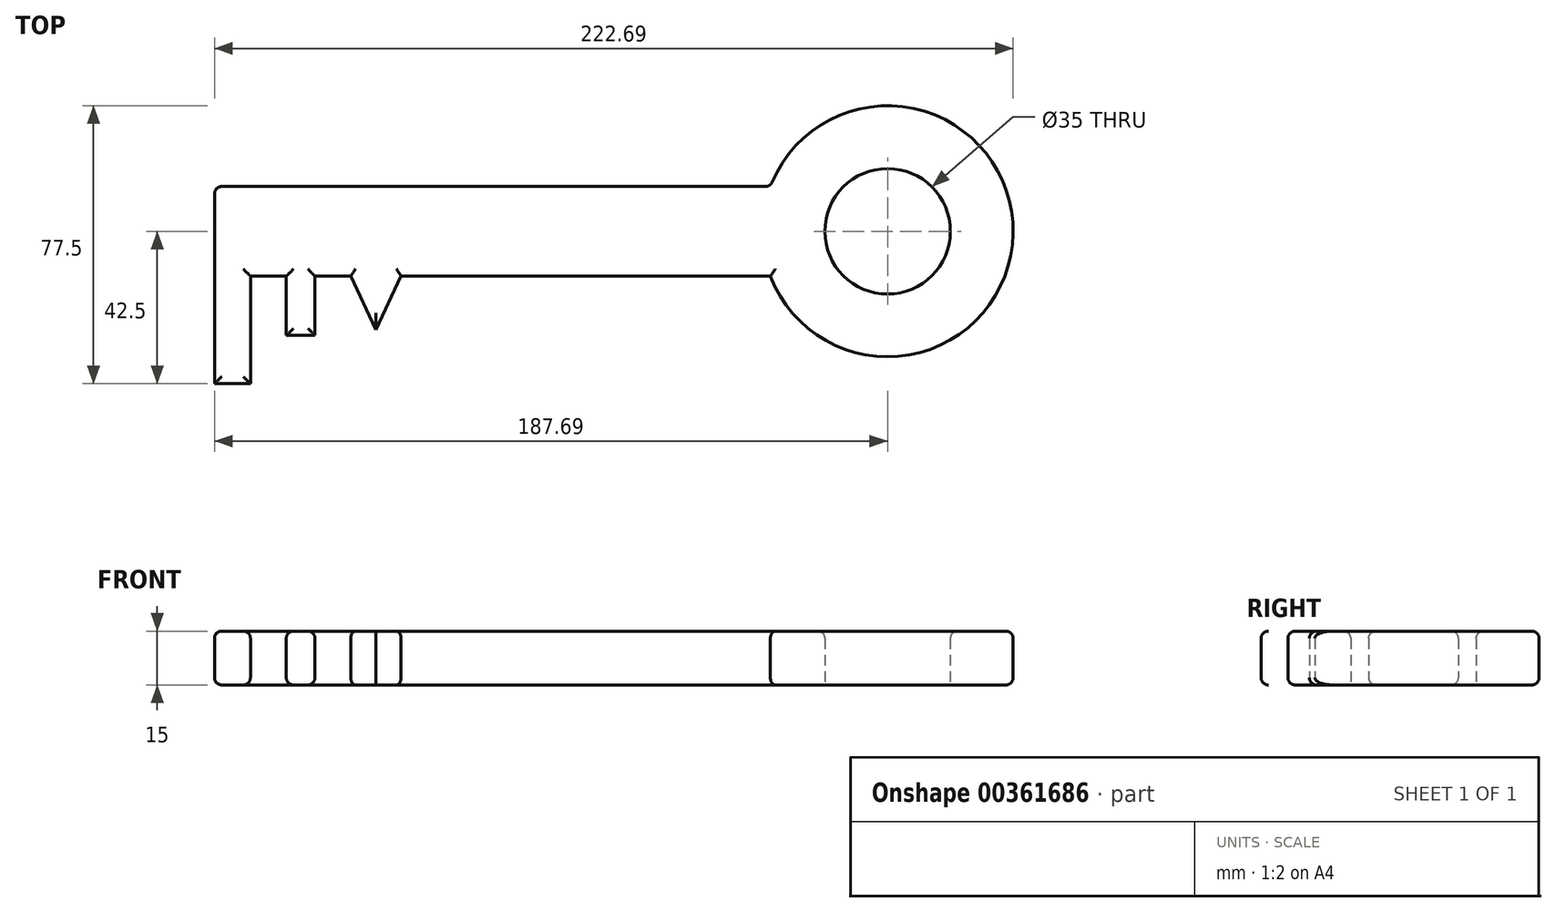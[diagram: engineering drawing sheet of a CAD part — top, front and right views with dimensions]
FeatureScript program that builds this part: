
annotation { "Feature Type Name" : "Feature", "Feature Type Description" : "" }
export const myFeature = defineFeature(function(context is Context, id is Id, definition is map)
    precondition{}
    {
        {
            var Q0;
            Q0=qCreatedBy(makeId("Top.planeOp"),FACE);
            var sketch = newSketch(context, id + "F0", { "sketchPlane" : qUnion([Q0])});
            skLineSegment(sketch, "E0.bottom", {"start": v(-68.81, 25) * mm, "end": v(86.19, 25) * mm});
            skLineSegment(sketch, "E0.top", {"start": v(-58.81, 0) * mm, "end": v(-48.81, 0) * mm});
            skLineSegment(sketch, "E0.left", {"start": v(-68.81, 25) * mm, "end": v(-68.81, 0) * mm});
            skLineSegment(sketch, "E1.top", {"start": v(-68.81, -30) * mm, "end": v(-58.81, -30) * mm});
            skLineSegment(sketch, "E1.left", {"start": v(-68.81, 0) * mm, "end": v(-68.81, -30) * mm});
            skLineSegment(sketch, "E1.right", {"start": v(-58.81, 0) * mm, "end": v(-58.81, -30) * mm});
            skLineSegment(sketch, "E2.top", {"start": v(-48.81, -16.55) * mm, "end": v(-40.81, -16.55) * mm});
            skLineSegment(sketch, "E2.left", {"start": v(-48.81, 0) * mm, "end": v(-48.81, -16.55) * mm});
            skLineSegment(sketch, "E2.right", {"start": v(-40.81, 0) * mm, "end": v(-40.81, -16.55) * mm});
            skArc(sketch, "E3", {"start": v(86.19, 0) * mm, "mid": v(153.88, 12.5) * mm, "end": v(86.19, 25) * mm});
            skCircle(sketch, "E4", {"center": v(118.88, 12.5) * mm, "radius": 17.5 * mm});
            skLineSegment(sketch, "E5", {"start": v(-16.81, 0) * mm, "end": v(-23.81, -15) * mm});
            skLineSegment(sketch, "E6", {"start": v(-30.81, 0) * mm, "end": v(-23.81, -15) * mm});
            skLineSegment(sketch, "E7", {"start": v(118.88, 12.5) * mm, "end": v(-68.81, 12.5) * mm, "construction": true});
            skLineSegment(sketch, "E8.trimOffspring", {"start": v(-40.81, 0) * mm, "end": v(-30.81, 0) * mm});
            skLineSegment(sketch, "E9.trimOffspring", {"start": v(-16.81, 0) * mm, "end": v(86.19, 0) * mm});
            skLineSegment(sketch, "E10", {"start": v(-30.81, 0) * mm, "end": v(-16.81, 0) * mm, "construction": true});
            skLineSegment(sketch, "E11", {"start": v(-23.81, -15) * mm, "end": v(-23.81, 0) * mm, "construction": true});
            skSolve(sketch);
        }
        {
            var Q0;
            Q0=makeQuery(id+"F0.imprint","IMPRINT",FACE,{"disambiguationData":[TD([[makeQuery(id+"F0.imprint","IMPRINT",EDGE,{"derivedFrom":sQuery(id+"F0.wireOp",EDGE,"E0.bottom")}),-1.0]])]});
            extrude(context, id + "F1", {"entities" : qUnion([Q0]), "depth" : 15 * mm});
        }
        {
            var Q0;
            Q0=makeQuery(id+"F1.opExtrude","CAP_EDGE",EDGE,{"disambiguationData":[OSD([sQuery(id+"F0.wireOp",EDGE,"E0.bottom")])],"isStart":false});
            var Q1;
            Q1=makeQuery(id+"F1.opExtrude","CAP_EDGE",EDGE,{"disambiguationData":[OSD([sQuery(id+"F0.wireOp",EDGE,"E0.left"),sQuery(id+"F0.wireOp",EDGE,"E1.left")])],"isStart":false});
            var Q2;
            Q2=makeQuery(id+"F1.opExtrude","CAP_EDGE",EDGE,{"disambiguationData":[OSD([sQuery(id+"F0.wireOp",EDGE,"E1.right")])],"isStart":false});
            var Q3;
            Q3=makeQuery(id+"F1.opExtrude","CAP_EDGE",EDGE,{"disambiguationData":[OSD([sQuery(id+"F0.wireOp",EDGE,"E2.left")])],"isStart":false});
            var Q4;
            Q4=makeQuery(id+"F1.opExtrude","CAP_EDGE",EDGE,{"disambiguationData":[OSD([sQuery(id+"F0.wireOp",EDGE,"E2.top")])],"isStart":false});
            var Q5;
            Q5=makeQuery(id+"F1.opExtrude","CAP_EDGE",EDGE,{"disambiguationData":[OSD([sQuery(id+"F0.wireOp",EDGE,"E6")])],"isStart":false});
            var Q6;
            Q6=makeQuery(id+"F1.opExtrude","CAP_EDGE",EDGE,{"disambiguationData":[OSD([sQuery(id+"F0.wireOp",EDGE,"E9.trimOffspring")])],"isStart":false});
            var Q7;
            Q7=makeQuery(id+"F1.opExtrude","CAP_EDGE",EDGE,{"disambiguationData":[OSD([sQuery(id+"F0.wireOp",EDGE,"E5")])],"isStart":false});
            var Q8;
            Q8=makeQuery(id+"F1.opExtrude","CAP_EDGE",EDGE,{"disambiguationData":[OSD([sQuery(id+"F0.wireOp",EDGE,"E2.right")])],"isStart":false});
            var Q9;
            Q9=makeQuery(id+"F1.opExtrude","CAP_EDGE",EDGE,{"disambiguationData":[OSD([sQuery(id+"F0.wireOp",EDGE,"E1.top")])],"isStart":false});
            var Q10;
            Q10=makeQuery(id+"F1.opExtrude","CAP_FACE",FACE,{"disambiguationData":[OSD([sQuery(id+"F0.wireOp",EDGE,"E0.bottom"),sQuery(id+"F0.wireOp",EDGE,"E0.top"),sQuery(id+"F0.wireOp",EDGE,"E0.left"),sQuery(id+"F0.wireOp",EDGE,"E1.top"),sQuery(id+"F0.wireOp",EDGE,"E1.left"),sQuery(id+"F0.wireOp",EDGE,"E1.right"),sQuery(id+"F0.wireOp",EDGE,"E2.top"),sQuery(id+"F0.wireOp",EDGE,"E2.left"),sQuery(id+"F0.wireOp",EDGE,"E2.right"),sQuery(id+"F0.wireOp",EDGE,"E3"),sQuery(id+"F0.wireOp",EDGE,"E4"),sQuery(id+"F0.wireOp",EDGE,"E5"),sQuery(id+"F0.wireOp",EDGE,"E6"),sQuery(id+"F0.wireOp",EDGE,"E8.trimOffspring"),sQuery(id+"F0.wireOp",EDGE,"E9.trimOffspring")])],"isStart":false});
            var Q11;
            Q11=makeQuery(id+"F1.opExtrude","CAP_EDGE",EDGE,{"disambiguationData":[OSD([sQuery(id+"F0.wireOp",EDGE,"E4")])],"isStart":false});
            var Q12;
            Q12=makeQuery(id+"F1.opExtrude","CAP_EDGE",EDGE,{"disambiguationData":[OSD([sQuery(id+"F0.wireOp",EDGE,"E3")])],"isStart":false});
            var Q13;
            Q13=makeQuery(id+"F1.opExtrude","CAP_EDGE",EDGE,{"disambiguationData":[OSD([sQuery(id+"F0.wireOp",EDGE,"E3")])],"isStart":true});
            var Q14;
            Q14=makeQuery(id+"F1.opExtrude","CAP_EDGE",EDGE,{"disambiguationData":[OSD([sQuery(id+"F0.wireOp",EDGE,"E0.bottom")])],"isStart":true});
            var Q15;
            Q15=makeQuery(id+"F1.opExtrude","SWEPT_EDGE",EDGE,{"disambiguationData":[OSD([sQuery(id+"F0.wireOp",EDGE,"E0.bottom"),sQuery(id+"F0.wireOp",EDGE,"E3")])]});
            var Q16;
            Q16=makeQuery(id+"F1.opExtrude","SWEPT_EDGE",EDGE,{"disambiguationData":[OSD([sQuery(id+"F0.wireOp",EDGE,"E0.bottom"),sQuery(id+"F0.wireOp",EDGE,"E0.left")])]});
            var Q17;
            Q17=makeQuery(id+"F1.opExtrude","CAP_EDGE",EDGE,{"disambiguationData":[OSD([sQuery(id+"F0.wireOp",EDGE,"E9.trimOffspring")])],"isStart":true});
            var Q18;
            Q18=makeQuery(id+"F1.opExtrude","CAP_EDGE",EDGE,{"disambiguationData":[OSD([sQuery(id+"F0.wireOp",EDGE,"E5")])],"isStart":true});
            var Q19;
            Q19=makeQuery(id+"F1.opExtrude","CAP_EDGE",EDGE,{"disambiguationData":[OSD([sQuery(id+"F0.wireOp",EDGE,"E6")])],"isStart":true});
            var Q20;
            Q20=makeQuery(id+"F1.opExtrude","CAP_EDGE",EDGE,{"disambiguationData":[OSD([sQuery(id+"F0.wireOp",EDGE,"E8.trimOffspring")])],"isStart":true});
            var Q21;
            Q21=makeQuery(id+"F1.opExtrude","CAP_EDGE",EDGE,{"disambiguationData":[OSD([sQuery(id+"F0.wireOp",EDGE,"E2.right")])],"isStart":true});
            var Q22;
            Q22=makeQuery(id+"F1.opExtrude","CAP_EDGE",EDGE,{"disambiguationData":[OSD([sQuery(id+"F0.wireOp",EDGE,"E2.top")])],"isStart":true});
            var Q23;
            Q23=makeQuery(id+"F1.opExtrude","CAP_EDGE",EDGE,{"disambiguationData":[OSD([sQuery(id+"F0.wireOp",EDGE,"E2.left")])],"isStart":true});
            var Q24;
            Q24=makeQuery(id+"F1.opExtrude","CAP_EDGE",EDGE,{"disambiguationData":[OSD([sQuery(id+"F0.wireOp",EDGE,"E0.top")])],"isStart":true});
            var Q25;
            Q25=makeQuery(id+"F1.opExtrude","CAP_EDGE",EDGE,{"disambiguationData":[OSD([sQuery(id+"F0.wireOp",EDGE,"E1.right")])],"isStart":true});
            var Q26;
            Q26=makeQuery(id+"F1.opExtrude","CAP_EDGE",EDGE,{"disambiguationData":[OSD([sQuery(id+"F0.wireOp",EDGE,"E1.top")])],"isStart":true});
            var Q27;
            Q27=makeQuery(id+"F1.opExtrude","CAP_EDGE",EDGE,{"disambiguationData":[OSD([sQuery(id+"F0.wireOp",EDGE,"E0.left"),sQuery(id+"F0.wireOp",EDGE,"E1.left")])],"isStart":true});
            fillet(context, id + "F2", {"entities" : qUnion([Q0, Q1, Q2, Q3, Q4, Q5, Q6, Q7, Q8, Q9, Q10, Q11, Q12, Q13, Q14, Q15, Q16, Q17, Q18, Q19, Q20, Q21, Q22, Q23, Q24, Q25, Q26, Q27]), "radius" : 2 * mm, "tangentPropagation" : true, "allowEdgeOverflow" : false});
        }
    });
